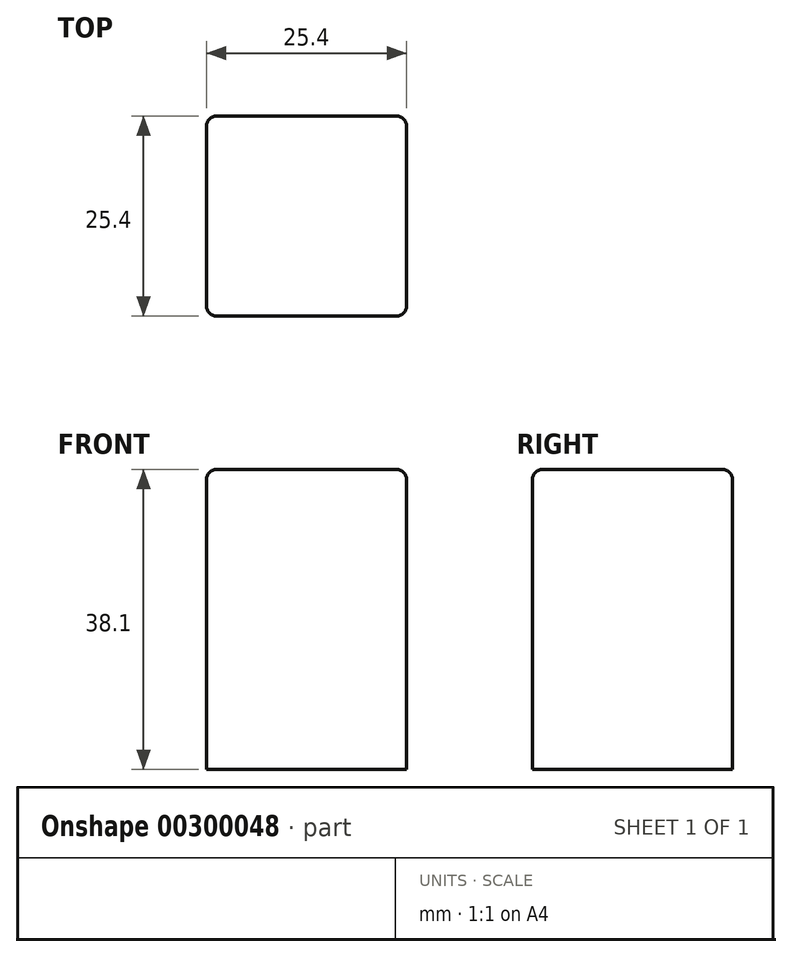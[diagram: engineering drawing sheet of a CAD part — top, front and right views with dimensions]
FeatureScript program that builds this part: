
annotation { "Feature Type Name" : "Feature", "Feature Type Description" : "" }
export const myFeature = defineFeature(function(context is Context, id is Id, definition is map)
    precondition{}
    {
        {
            var Q0;
            Q0=qCreatedBy(makeId("Top.planeOp"),FACE);
            var sketch = newSketch(context, id + "F0", { "sketchPlane" : qUnion([Q0])});
            skLineSegment(sketch, "E0.bottom", {"start": v(12.7, 12.7) * mm, "end": v(-12.7, 12.7) * mm});
            skLineSegment(sketch, "E0.top", {"start": v(12.7, -12.7) * mm, "end": v(-12.7, -12.7) * mm});
            skLineSegment(sketch, "E0.left", {"start": v(12.7, 12.7) * mm, "end": v(12.7, -12.7) * mm});
            skLineSegment(sketch, "E0.right", {"start": v(-12.7, 12.7) * mm, "end": v(-12.7, -12.7) * mm});
            skPoint(sketch, "E0.middle", {"position": v(0, 0) * mm});
            skSolve(sketch);
        }
        {
            var Q0;
            Q0 = qSketchRegion(id + "F0", true);
            extrude(context, id + "F1", {"entities" : qUnion([Q0]), "endBound" : BoundingType.SYMMETRIC, "depth" : 38.1 * mm});
        }
        {
            var Q0;
            Q0=makeQuery(id+"F1.opExtrude","CAP_EDGE",EDGE,{"disambiguationData":[OSD([sQuery(id+"F0.wireOp",EDGE,"E0.top")])],"isStart":false});
            var Q1;
            Q1=makeQuery(id+"F1.opExtrude","CAP_EDGE",EDGE,{"disambiguationData":[OSD([sQuery(id+"F0.wireOp",EDGE,"E0.left")])],"isStart":false});
            var Q2;
            Q2=makeQuery(id+"F1.opExtrude","SWEPT_EDGE",EDGE,{"disambiguationData":[OSD([sQuery(id+"F0.wireOp",EDGE,"E0.top"),sQuery(id+"F0.wireOp",EDGE,"E0.left")])]});
            var Q3;
            Q3=makeQuery(id+"F1.opExtrude","CAP_EDGE",EDGE,{"disambiguationData":[OSD([sQuery(id+"F0.wireOp",EDGE,"E0.bottom")])],"isStart":false});
            var Q4;
            Q4=makeQuery(id+"F1.opExtrude","CAP_EDGE",EDGE,{"disambiguationData":[OSD([sQuery(id+"F0.wireOp",EDGE,"E0.right")])],"isStart":false});
            var Q5;
            Q5=makeQuery(id+"F1.opExtrude","SWEPT_EDGE",EDGE,{"disambiguationData":[OSD([sQuery(id+"F0.wireOp",EDGE,"E0.top"),sQuery(id+"F0.wireOp",EDGE,"E0.right")])]});
            var Q6;
            Q6=makeQuery(id+"F1.opExtrude","SWEPT_EDGE",EDGE,{"disambiguationData":[OSD([sQuery(id+"F0.wireOp",EDGE,"E0.bottom"),sQuery(id+"F0.wireOp",EDGE,"E0.right")])]});
            var Q7;
            Q7=makeQuery(id+"F1.opExtrude","SWEPT_EDGE",EDGE,{"disambiguationData":[OSD([sQuery(id+"F0.wireOp",EDGE,"E0.bottom"),sQuery(id+"F0.wireOp",EDGE,"E0.left")])]});
            fillet(context, id + "F2", {"entities" : qUnion([Q0, Q1, Q2, Q3, Q4, Q5, Q6, Q7]), "radius" : 1.27 * mm, "tangentPropagation" : true, "allowEdgeOverflow" : false});
        }
    });
